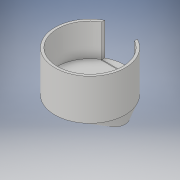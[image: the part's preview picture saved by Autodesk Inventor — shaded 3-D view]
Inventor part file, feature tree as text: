
AUTODESK INVENTOR PART (.ipt)
format: ipt  version: 2019 (Build 230136000, 136)  size: 248,320 bytes
history: native  units: mm
features: sketch x6, extrude x4, fillet x3, loft x2, other x2, plane x1
ambient origin geometry x8: Origin, YZ Plane, XZ Plane, XY Plane, X Axis, Y Axis, Z Axis, Center Point
bodies: Solid1 (feature_tree)
feature tree (18):
  extrude  "Extrusion1"  Depth=86.0mm
  extrude  "Extrusion2"  Depth=1.0mm
  extrude  "Extrusion3"  Depth=40.0mm
  sketch  "Sketch9"  dims[d7=80.0mm d8=10.0mm d9=0.0mm]
  plane  "Work Plane2"
  loft  "Loft1"
  extrude  "Extrusion6"  Depth=40.0mm
  loft  "Loft2"
  fillet  "Fillet1"  [1 undecoded]
  fillet  "Fillet2"  Radius=20.0mm
  fillet  "Fillet3"  Radius=20.0mm
  sketch  "Sketch1"  dims[d0=80.0mm d1=86.0mm]
  sketch  "Sketch2"  dims[d2=40.0mm d3=0.0mm d4=1.0mm]
  sketch  "Sketch3"  dims[d5=1.0mm d6=40.0mm]
  sketch  "Sketch10"  dims[d10=10.0mm d11=0.0mm d21=40.0mm]
  sketch  "Sketch11"  dims[d22=26.0mm d23=0.0mm d24=90.0deg d25=0.0mm d26=90.0deg d27=20.0mm d28=20.0mm d29=0.0mm d30=0.0mm d31=90.0deg d32=0.0mm d33=90.0deg d34=10.0mm d35=10.0mm d36=86.0mm d37=86.0mm d38=43.0mm d39=86.0mm d40=5.0mm]
  other  "Edges1"
  other  "Edges2"
note: 1 required parameter value undecoded (feature->parameter linkage not recoverable at this tier; creation-order binding heuristic only, values carry confidence <= 0.55)
